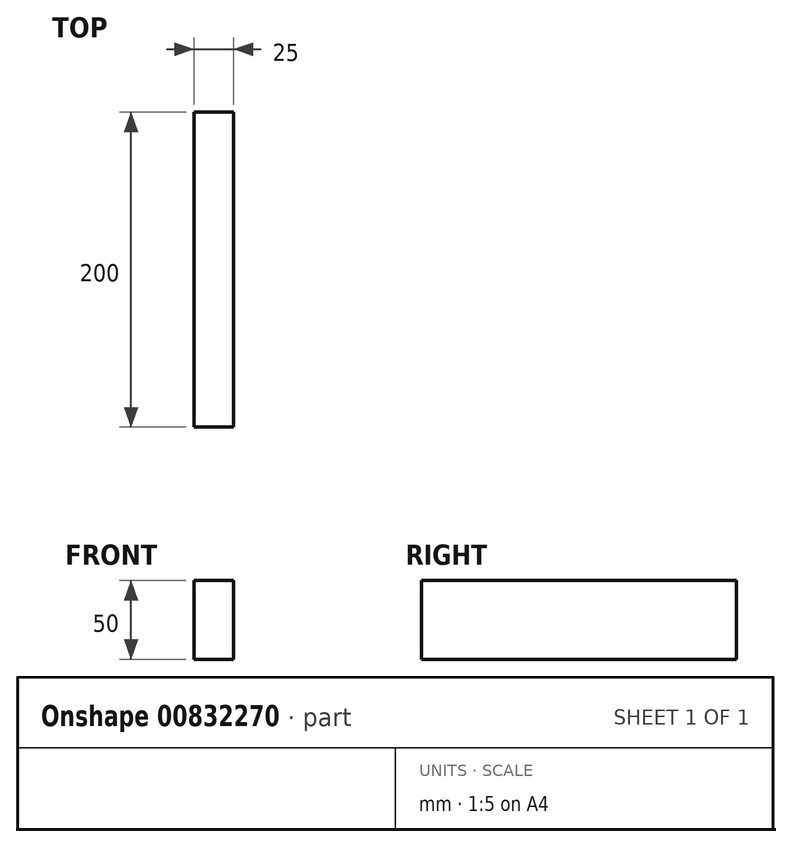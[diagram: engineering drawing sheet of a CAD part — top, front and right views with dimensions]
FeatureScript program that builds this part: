
annotation { "Feature Type Name" : "Feature", "Feature Type Description" : "" }
export const myFeature = defineFeature(function(context is Context, id is Id, definition is map)
    precondition{}
    {
        {
            var Q0;
            Q0=qCreatedBy(makeId("Right.planeOp"),FACE);
            var sketch = newSketch(context, id + "F0", { "sketchPlane" : qUnion([Q0])});
            skLineSegment(sketch, "E0.bottom", {"start": v(0, 0) * mm, "end": v(200, 0) * mm});
            skLineSegment(sketch, "E0.top", {"start": v(0, -50) * mm, "end": v(200, -50) * mm});
            skLineSegment(sketch, "E0.left", {"start": v(0, 0) * mm, "end": v(0, -50) * mm});
            skLineSegment(sketch, "E0.right", {"start": v(200, 0) * mm, "end": v(200, -50) * mm});
            skSolve(sketch);
        }
        {
            var Q0;
            Q0=makeQuery(id+"F0.imprint","IMPRINT",FACE,{"disambiguationData":[TD([[makeQuery(id+"F0.imprint","IMPRINT",EDGE,{"derivedFrom":sQuery(id+"F0.wireOp",EDGE,"E0.bottom")}),-1.0]])]});
            extrude(context, id + "F1", {"entities" : qUnion([Q0]), "depth" : 25 * mm, "offsetDistance" : 25 * mm});
        }
    });
